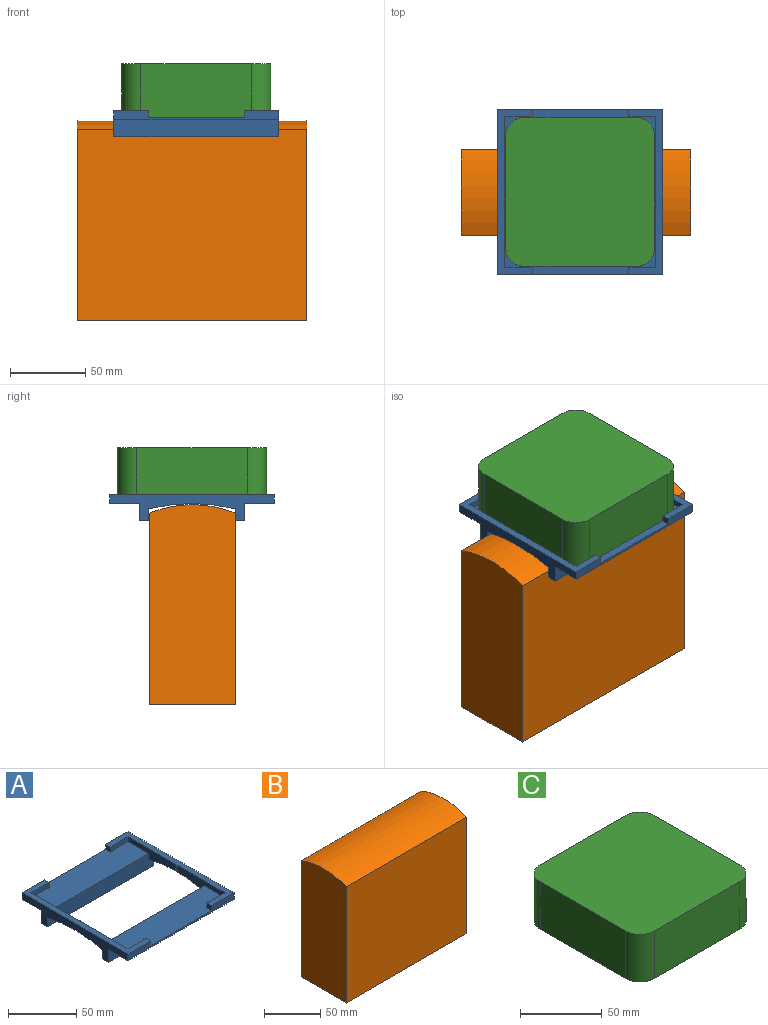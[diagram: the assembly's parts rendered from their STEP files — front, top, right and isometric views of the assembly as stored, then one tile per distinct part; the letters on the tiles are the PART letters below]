
ASSEMBLY  parts=3 mates=4
PART A: 44 faces, bbox 109.6x109.6x17.5 mm
  f0: plane 100.33x9.53mm, normal (-1,0,0), area 596mm2, adj f2,f3,f4,f5,f6,f11,f13,f14
  f1: plane 100.33x9.53mm, normal (1,0,0), area 596mm2, adj f3,f5,f7,f13,f14,f18,f23,f24
  f2: plane 17.15x4.45mm, normal (0,1,0), area 76.3mm2, adj f0,f3,f11,f34
  f3: plane 100.33x26.07mm, normal (0,0,1), area 2444.5mm2, adj f0,f1,f2,f13,f21,f24,f25,f26
  f4: plane 17.15x4.45mm, normal (0,-1,0), area 76.3mm2, adj f0,f5,f11,f31
  f5: plane 100.33x26.07mm, normal (0,0,1), area 2444.5mm2, adj f0,f1,f4,f8,f14,f22,f23,f27
  f6: cylinder r=117.85mm len=57.4mm, axis (-1,0,0), area 267.3mm2, adj f0,f13,f14,f16
  f7: plane 109.55x23.03mm, normal (0,0,1), area 677.2mm2, adj f1,f8,f17,f21,f22,f23,f24,f25
  f8: plane 109.55x5.98mm, normal (0,1,0), area 372mm2, adj f5,f7,f11,f16,f17,f19,f22,f27
  f9: plane 109.55x11.49mm, normal (0,-1,0), area 1258.3mm2, adj f12,f16,f17,f20
  f10: plane 109.55x11.49mm, normal (0,1,0), area 1258.3mm2, adj f15,f16,f17,f19
  f11: plane 109.55x23.03mm, normal (0,0,1), area 677.2mm2, adj f0,f2,f4,f8,f16,f21,f26,f27
  f12: plane 109.55x6.35mm, normal (0,0,-1), area 695.6mm2, adj f9,f13,f16,f17
  f13: plane 109.55x13.01mm, normal (0,1,0), area 1378.5mm2, adj f0,f1,f3,f6,f12,f16,f17,f18
  f14: plane 109.55x13.01mm, normal (0,-1,0), area 1378.5mm2, adj f0,f1,f5,f6,f15,f16,f17,f18
  f15: plane 109.55x6.35mm, normal (0,0,-1), area 695.6mm2, adj f10,f14,f16,f17
  f16: plane 109.55x17.46mm, normal (1,0,0), area 868.1mm2, adj f6,f8,f9,f10,f11,f12,f13,f14
  f17: plane 109.55x17.46mm, normal (-1,0,0), area 868.1mm2, adj f7,f8,f9,f10,f12,f13,f14,f15
  f18: cylinder r=117.85mm len=57.4mm, axis (-1,0,0), area 267.3mm2, adj f1,f13,f14,f17
  f19: plane 109.55x19.72mm, normal (0,0,-1), area 2160.7mm2, adj f8,f10,f16,f17
  f20: plane 109.55x19.72mm, normal (0,0,-1), area 2160.7mm2, adj f9,f16,f17,f21
  f21: plane 109.55x5.98mm, normal (0,-1,0), area 372mm2, adj f3,f7,f11,f16,f17,f20,f25,f26
  f22: plane 5.25x4.45mm, normal (1,0,0), area 23.4mm2, adj f5,f7,f8,f29
  f23: plane 17.15x4.45mm, normal (0,-1,0), area 76.3mm2, adj f1,f5,f7,f28
  f24: plane 17.15x4.45mm, normal (0,1,0), area 76.3mm2, adj f1,f3,f7,f33
  f25: plane 5.25x4.45mm, normal (1,0,0), area 23.4mm2, adj f3,f7,f21,f32
  f26: plane 5.25x4.45mm, normal (-1,0,0), area 23.4mm2, adj f3,f11,f21,f35
  f27: plane 5.25x4.45mm, normal (-1,0,0), area 23.4mm2, adj f5,f8,f11,f30
  f28: plane 4.45x0.64mm, normal (-1,0,0), area 2.8mm2, adj f5,f7,f23,f29
  f29: plane 4.45x1.27mm, normal (0,-1,0), area 5.7mm2, adj f5,f7,f22,f28
  f30: plane 4.45x1.27mm, normal (0,-1,0), area 5.7mm2, adj f5,f11,f27,f31
  f31: plane 4.45x0.64mm, normal (1,0,0), area 2.8mm2, adj f4,f5,f11,f30
  f32: plane 4.45x1.27mm, normal (0,1,0), area 5.7mm2, adj f3,f7,f25,f33
  f33: plane 4.45x0.64mm, normal (-1,0,0), area 2.8mm2, adj f3,f7,f24,f32
  f34: plane 4.45x0.64mm, normal (1,0,0), area 2.8mm2, adj f2,f3,f11,f35
  f35: plane 4.45x1.27mm, normal (0,1,0), area 5.7mm2, adj f3,f11,f26,f34
  f36: plane 4.45x0.64mm, normal (0,-1,0), area 2.8mm2, adj f1,f7,f37,f38
  f37: plane 1.27x0.64mm, normal (0,0,-1), area 0.8mm2, adj f1,f36,f38,f39
  f38: plane 4.45x1.27mm, normal (1,0,0), area 5.7mm2, adj f7,f36,f37,f39
  f39: plane 4.45x0.64mm, normal (0,1,0), area 2.8mm2, adj f1,f7,f37,f38
  f40: plane 1.27x0.64mm, normal (0,0,-1), area 0.8mm2, adj f0,f41,f42,f43
  f41: plane 4.45x0.64mm, normal (0,1,0), area 2.8mm2, adj f0,f11,f40,f43
  f42: plane 4.45x0.64mm, normal (0,-1,0), area 2.8mm2, adj f0,f11,f40,f43
  f43: plane 4.45x1.27mm, normal (-1,0,0), area 5.7mm2, adj f11,f40,f41,f42
PART B: 6 faces, bbox 152.4x57.2x132.6 mm
  f0: plane 152.4x57.15mm, normal (0,0,-1), area 8709.7mm2, adj f1,f3,f4,f5
  f1: plane 152.4x127mm, normal (0,1,0), area 19354.8mm2, adj f0,f2,f4,f5
  f2: cylinder r=76.2mm len=152.4mm, axis (-1,0,0), area 8927.9mm2, adj f1,f3,f4,f5
  f3: plane 152.4x127mm, normal (0,-1,0), area 19354.8mm2, adj f0,f2,f4,f5
  f4: plane 132.56x57.15mm, normal (1,0,0), area 7471.5mm2, adj f0,f1,f2,f3
  f5: plane 132.56x57.15mm, normal (-1,0,0), area 7471.5mm2, adj f0,f1,f2,f3
PART C: 15 faces, bbox 99.1x99.1x35.6 mm
  f0: plane 73.66x35.56mm, normal (0,1,0), area 2296.8mm2, adj f4,f5,f6,f7,f10,f11,f12,f13
  f1: plane 73.66x35.56mm, normal (1,0,0), area 2619.3mm2, adj f4,f5,f6,f9
  f2: plane 73.66x35.56mm, normal (-1,0,0), area 2619.3mm2, adj f4,f5,f7,f8
  f3: plane 73.66x35.56mm, normal (0,-1,0), area 2619.3mm2, adj f4,f5,f8,f9
  f4: plane 99.06x99.06mm, normal (0,0,1), area 9674.4mm2, adj f0,f1,f2,f3,f6,f7,f8,f9
  f5: plane 99.06x99.06mm, normal (0,0,-1), area 9674.4mm2, adj f0,f1,f2,f3,f6,f7,f8,f9
  f6: cylinder r=12.7mm len=35.56mm, axis (0,0,1), area 709.4mm2, adj f0,f1,f4,f5
  f7: cylinder r=12.7mm len=35.56mm, axis (0,0,-1), area 709.4mm2, adj f0,f2,f4,f5
  f8: cylinder r=12.7mm len=35.56mm, axis (0,0,1), area 709.4mm2, adj f2,f3,f4,f5
  f9: cylinder r=12.7mm len=35.56mm, axis (0,0,-1), area 709.4mm2, adj f1,f3,f4,f5
  f10: plane 12.7x2.54mm, normal (1,0,0), area 32.3mm2, adj f0,f11,f13,f14
  f11: plane 25.4x2.54mm, normal (0,0,-1), area 64.5mm2, adj f0,f10,f12,f14
  f12: plane 12.7x2.54mm, normal (-1,0,0), area 32.3mm2, adj f0,f11,f13,f14
  f13: plane 25.4x2.54mm, normal (0,0,1), area 64.5mm2, adj f0,f10,f12,f14
  f14: plane 25.4x12.7mm, normal (0,1,0), area 322.6mm2, adj f10,f11,f12,f13
PLACE A t=(-25.28,41.42,68.26)mm
PLACE B t=(-28.1,41.29,1.95)mm fixed
PLACE C t=(-25.28,41.42,73.33)mm
MATE planar A.f5 <-> C.f5  axis (0,0,1) through (-25.28,82.41,73.33)mm
MATE planar C.f1 <-> A.f43  axis (1,0,0) through (24.25,41.42,91.11)mm
MATE planar B.f3 <-> A.f13  axis (0,-1,0) through (-28.1,12.72,1.95)mm
MATE planar C.f3 <-> A.f35  axis (0,-1,0) through (-25.28,-8.11,91.11)mm
